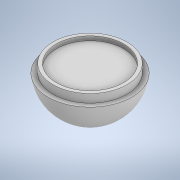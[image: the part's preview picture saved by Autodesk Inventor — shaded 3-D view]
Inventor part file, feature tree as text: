
AUTODESK INVENTOR PART (.ipt)
format: ipt  version: 2022 (Build 260153000, 153)  size: 138,752 bytes
history: native  units: in
note: dims shown in document units (in); Inventor stores cm internally (conversion verified against a paired STEP export)
features: sketch x3, extrude x2, revolve x1
ambient origin geometry x8: Origin, YZ Plane, XZ Plane, XY Plane, X Axis, Y Axis, Z Axis, Center Point
bodies: Solid1 (feature_tree)
feature tree (6):
  revolve  "Revolution1"  Angle=180.0deg
  extrude  "Extrusion1"  Depth=1.1in
  extrude  "Extrusion2"  Depth=0.125in TaperAngle=0.0deg
  sketch  "Sketch1"  dims[d0=1.25in d1=180.0deg]
  sketch  "Sketch2"  dims[d2=180.0deg d3=1.1in]
  sketch  "Sketch3"  dims[d4=1.0in d5=0.125in d6=0.0in d7=0.125in d8=0.0in]
